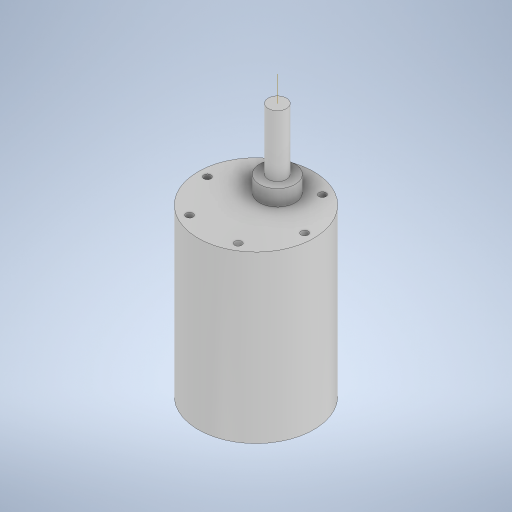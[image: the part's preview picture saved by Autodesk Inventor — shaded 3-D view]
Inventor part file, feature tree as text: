
AUTODESK INVENTOR PART (.ipt)
format: ipt  version: 2024 (Build 280153000, 153)  size: 269,312 bytes
history: native  units: in
note: dims shown in document units (in); Inventor stores cm internally (conversion verified against a paired STEP export)
features: extrude x4, sketch x4, projected_geometry x2, other x1
ambient origin geometry x8: Origin, YZ Plane, XZ Plane, XY Plane, X Axis, Y Axis, Z Axis, Center Point
bodies: Solid1 (feature_tree)
feature tree (11):
  extrude  "Extrusion1"  Depth=2.08in TaperAngle=0.0deg
  extrude  "Extrusion2"  Depth=0.2in TaperAngle=0.0deg
  extrude  "Extrusion3"  Depth=0.77in TaperAngle=0.0deg
  other  "Work Axis1"
  extrude  "Extrusion4"  Depth=0.3in
  sketch  "Sketch1"  dims[d0=1.45in d1=2.08in d2=0.0in]
  sketch  "Sketch2"  dims[d3=0.446in d4=0.2in d5=0.0in]
  sketch  "Sketch3"  dims[d6=0.23in d7=0.77in d8=0.0in]
  projected_geometry  "Projected Loop1"
  sketch  "Sketch4"  dims[d10=0.77in d11=0.09in d12=2.3622in d14=360.0deg d16=0.07in d17=0.3in d18=0.0in]
  projected_geometry  "Projected Loop2"
